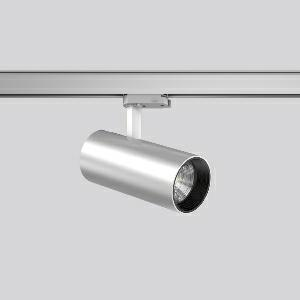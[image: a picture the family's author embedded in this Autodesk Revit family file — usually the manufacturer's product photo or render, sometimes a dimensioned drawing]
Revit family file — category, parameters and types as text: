
# Revit family: deecos_s_mini_742201_004_76_08e5
name_source: partatom
category: Lighting Fixtures
units: mm (PartAtom-declared; Revit-internal decimal feet)

## family parameters
Cut with Voids When Loaded = No
Host = Face
Light Source = No
Part Type = Normal
Room Calculation Point = No
Round Connector Dimension = Use Diameter
Shared = No

## types (1)
- DEECOS S mini (1 x LED Modul 930, 2250 lm, 3000)
    Apparent Load = 20 VA
    Approval mark = CE
    CIE Flux Codes = 80 99 100 100 100
    Color Rendering = 90
    Color Temperature = 3000
    Default Elevation = 1800 mm
    Description = Series: DEECOS S mini
LED surface-mounted projector in modern design with no visible cooling ribs. Housing: die-cast aluminium, powder-coated. Rotation range: 356°. Swivel range: 90°. Black plastic ring and recessed LED to prevent glare from the side. Optical assembly with lens made of plastic (polycarbonate) for the best homogeneous light distribution - can be changed without tools. Best colour rendering index Ra>90. With adapter for RZB 3-circuit DALI tracks. Suitable for Track on ceiling, Wall track. High quality converter without flickering and stroboscopic effect. The following accessories can be mounted without use of tools: interchangeable lenses, decorative glasses, honeycomb louvre, clear and frosted diffusers, white interchangeable plastic ring. 
Colour: silver
Diameter: 87 mm
Height: 214 mm
Lamp: LED
Socket: without socket
Colour temperature: 3000K
Colour rendering index (CRI): 92
System power: 20 W
Rated luminous flux: 2250 lm
Luminous efficiency: 113 lm/W
Control gear: Converter, dimmable, DALI
Protection class: I
Type of protection: IP 20
    Height = 214 mm
    Lamp = 1 x LED Modul 930
    Lamp Light Flux = 2250 lm
    Lamp count = 1
    Length = 87 mm
    Lifetime = 50000 h
    Luminous efficacy = 113 lm/W
    Manufacturer = RZB
    ModVariant = No
    Model = 742201.004.76
    Mounting Place = Ceiling
    Mounting Type = Rail mounted
    Number of Poles = 1
    OnlyDefault = Yes
    Power Factor = 1
    Product Name = DEECOS S mini
    Product group = Track mounted projectors
    ProductGroupID = 301
    Protection Class = Protection class I
    Protection Degree = IP 20
    RLX_Detail_Level = 1
    RLX_Emergency_Light_Flux = 0 lm
    RLX_Emergency_Type = 0
    RLX_Emergency_Type_DB = No
    RlxData = <blob elided: 37353 chars, md5=38ab0471>
    Socket = socket
    Standby Power = 0 W
    System Light Flux = 2250 lm
    System Power = 20 W
    Type Comments = Product without accessories
    Type Image = 741930.004.jpg
    URL = http://relux.com
    VarID = ---
    Voltage = 230 V
    Voltage Range = 220-240 V
    Weight = 0.00 kg
    Width = 0 mm  [stored 0 ft]

note: [stored X ft] marks values corroborated as IEEE doubles in the binary element streams (Revit-internal decimal feet)

## geometry (parser evidence)
native form markers: Blend x4, Sweep x12
no freeform markers — native parametric forms only
